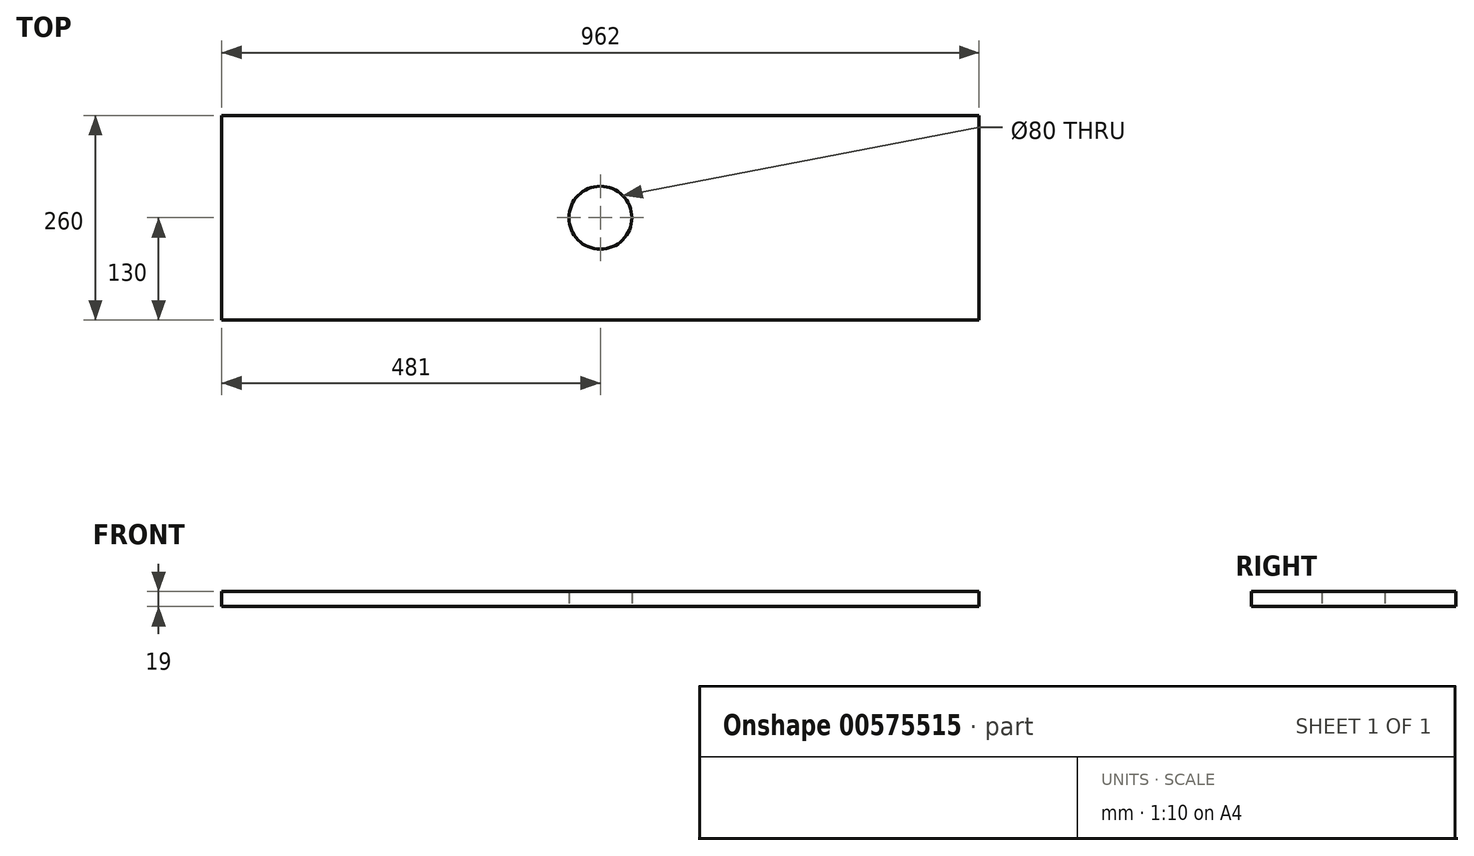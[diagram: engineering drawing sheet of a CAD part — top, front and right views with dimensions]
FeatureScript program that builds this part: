
annotation { "Feature Type Name" : "Feature", "Feature Type Description" : "" }
export const myFeature = defineFeature(function(context is Context, id is Id, definition is map)
    precondition{}
    {
        {
            var Q0;
            Q0=qCreatedBy(makeId("Top.planeOp"),FACE);
            var sketch = newSketch(context, id + "F0", { "sketchPlane" : qUnion([Q0])});
            skPoint(sketch, "E0.middle", {"position": v(0, 0) * mm});
            skLineSegment(sketch, "E1.bottom", {"start": v(500, 170) * mm, "end": v(-500, 170) * mm});
            skLineSegment(sketch, "E1.top", {"start": v(500, -170) * mm, "end": v(-500, -170) * mm});
            skLineSegment(sketch, "E1.left", {"start": v(500, 170) * mm, "end": v(500, -170) * mm});
            skLineSegment(sketch, "E1.right", {"start": v(-500, 170) * mm, "end": v(-500, -170) * mm});
            skLineSegment(sketch, "E2.bottom", {"start": v(-481, 130) * mm, "end": v(481, 130) * mm});
            skLineSegment(sketch, "E2.top", {"start": v(-481, -130) * mm, "end": v(481, -130) * mm});
            skLineSegment(sketch, "E2.left", {"start": v(-481, 130) * mm, "end": v(-481, -130) * mm});
            skLineSegment(sketch, "E2.right", {"start": v(481, 130) * mm, "end": v(481, -130) * mm});
            skCircle(sketch, "E3", {"center": v(0, 0) * mm, "radius": 40 * mm});
            skSolve(sketch);
        }
        {
            var Q0;
            Q0=makeQuery(id+"F0.imprint","IMPRINT",FACE,{"disambiguationData":[TD([[makeQuery(id+"F0.imprint","IMPRINT",EDGE,{"derivedFrom":sQuery(id+"F0.wireOp",EDGE,"E2.bottom")}),-1.0]])]});
            extrude(context, id + "F1", {"entities" : qUnion([Q0]), "depth" : 19 * mm, "offsetDistance" : 25 * mm});
        }
    });
